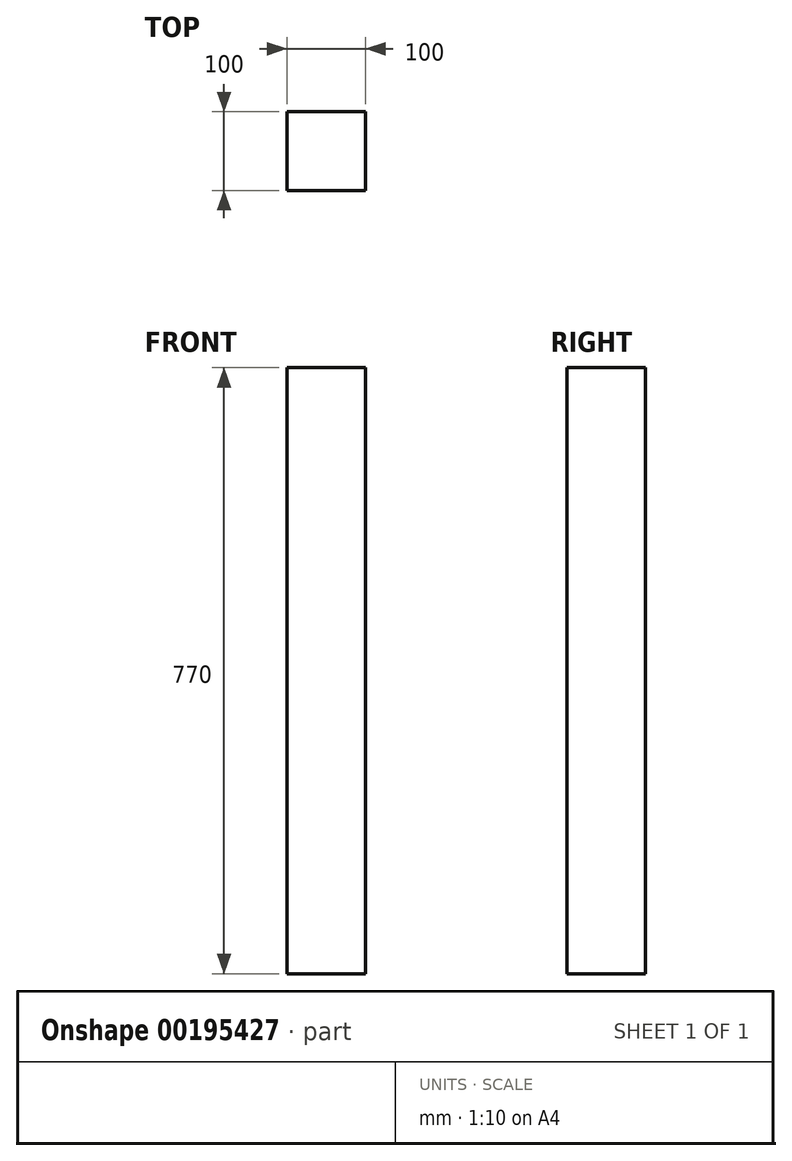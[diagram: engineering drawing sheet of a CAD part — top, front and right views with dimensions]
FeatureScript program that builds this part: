
annotation { "Feature Type Name" : "Feature", "Feature Type Description" : "" }
export const myFeature = defineFeature(function(context is Context, id is Id, definition is map)
    precondition{}
    {
        {
            var Q0;
            Q0=qCreatedBy(makeId("Top.planeOp"),FACE);
            var sketch = newSketch(context, id + "F0", { "sketchPlane" : qUnion([Q0])});
            skLineSegment(sketch, "E0.bottom", {"start": v(50, -50) * mm, "end": v(-50, -50) * mm});
            skLineSegment(sketch, "E0.top", {"start": v(50, 50) * mm, "end": v(-50, 50) * mm});
            skLineSegment(sketch, "E0.left", {"start": v(50, -50) * mm, "end": v(50, 50) * mm});
            skLineSegment(sketch, "E0.right", {"start": v(-50, -50) * mm, "end": v(-50, 50) * mm});
            skPoint(sketch, "E0.middle", {"position": v(0, 0) * mm});
            skSolve(sketch);
        }
        {
            var Q0;
            Q0=makeQuery(id+"F0.imprint","IMPRINT",FACE,{"disambiguationData":[TD([[makeQuery(id+"F0.imprint","IMPRINT",EDGE,{"derivedFrom":sQuery(id+"F0.wireOp",EDGE,"E0.bottom")}),-1.0]])]});
            extrude(context, id + "F1", {"entities" : qUnion([Q0]), "depth" : 770 * mm});
        }
    });
